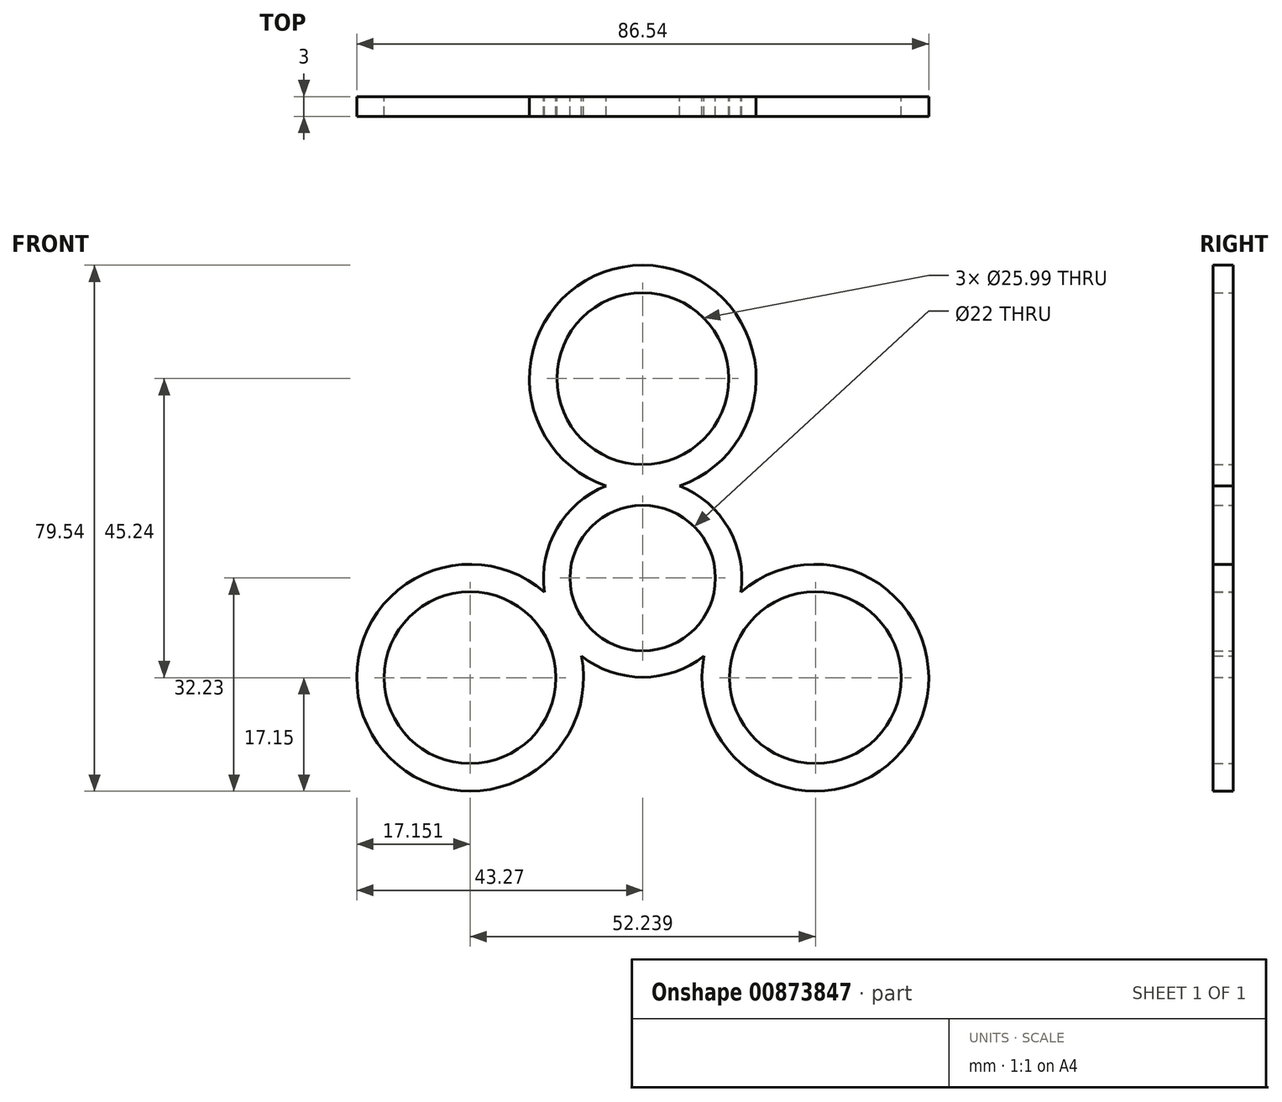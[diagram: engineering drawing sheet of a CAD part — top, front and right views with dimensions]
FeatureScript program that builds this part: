
annotation { "Feature Type Name" : "Feature", "Feature Type Description" : "" }
export const myFeature = defineFeature(function(context is Context, id is Id, definition is map)
    precondition{}
    {
        {
            var Q0;
            Q0=qCreatedBy(makeId("Front.planeOp"),FACE);
            var sketch = newSketch(context, id + "F0", { "sketchPlane" : qUnion([Q0])});
            skCircle(sketch, "E0", {"center": v(0, 0) * mm, "radius": 11 * mm});
            skArc(sketch, "E1", {"start": v(-5.56, 13.93) * mm, "mid": v(-13, 7.5) * mm, "end": v(-14.84, -2.15) * mm});
            skCircle(sketch, "E2", {"center": v(0, 30.16) * mm, "radius": 13 * mm});
            skArc(sketch, "E3", {"start": v(5.56, 13.93) * mm, "mid": v(0, 47.31) * mm, "end": v(-5.56, 13.93) * mm});
            skArc(sketch, "E4.1.0", {"start": v(-14.84, -2.15) * mm, "mid": v(-40.97, -23.66) * mm, "end": v(-9.29, -11.78) * mm});
            skArc(sketch, "E4.1.1", {"start": v(-9.29, -11.78) * mm, "mid": v(0, -15) * mm, "end": v(9.29, -11.78) * mm});
            skCircle(sketch, "E4.1.2", {"center": v(-26.12, -15.08) * mm, "radius": 13 * mm});
            skArc(sketch, "E4.2.0", {"start": v(9.29, -11.78) * mm, "mid": v(40.97, -23.66) * mm, "end": v(14.84, -2.15) * mm});
            skArc(sketch, "E4.2.1", {"start": v(14.84, -2.15) * mm, "mid": v(13, 7.5) * mm, "end": v(5.56, 13.93) * mm});
            skCircle(sketch, "E4.2.2", {"center": v(26.12, -15.08) * mm, "radius": 13 * mm});
            skSolve(sketch);
        }
        {
            var Q0;
            Q0 = qSketchRegion(id + "F0", true);
            extrude(context, id + "F1", {"entities" : qUnion([Q0]), "depth" : 3 * mm, "offsetDistance" : 25 * mm});
        }
    });
